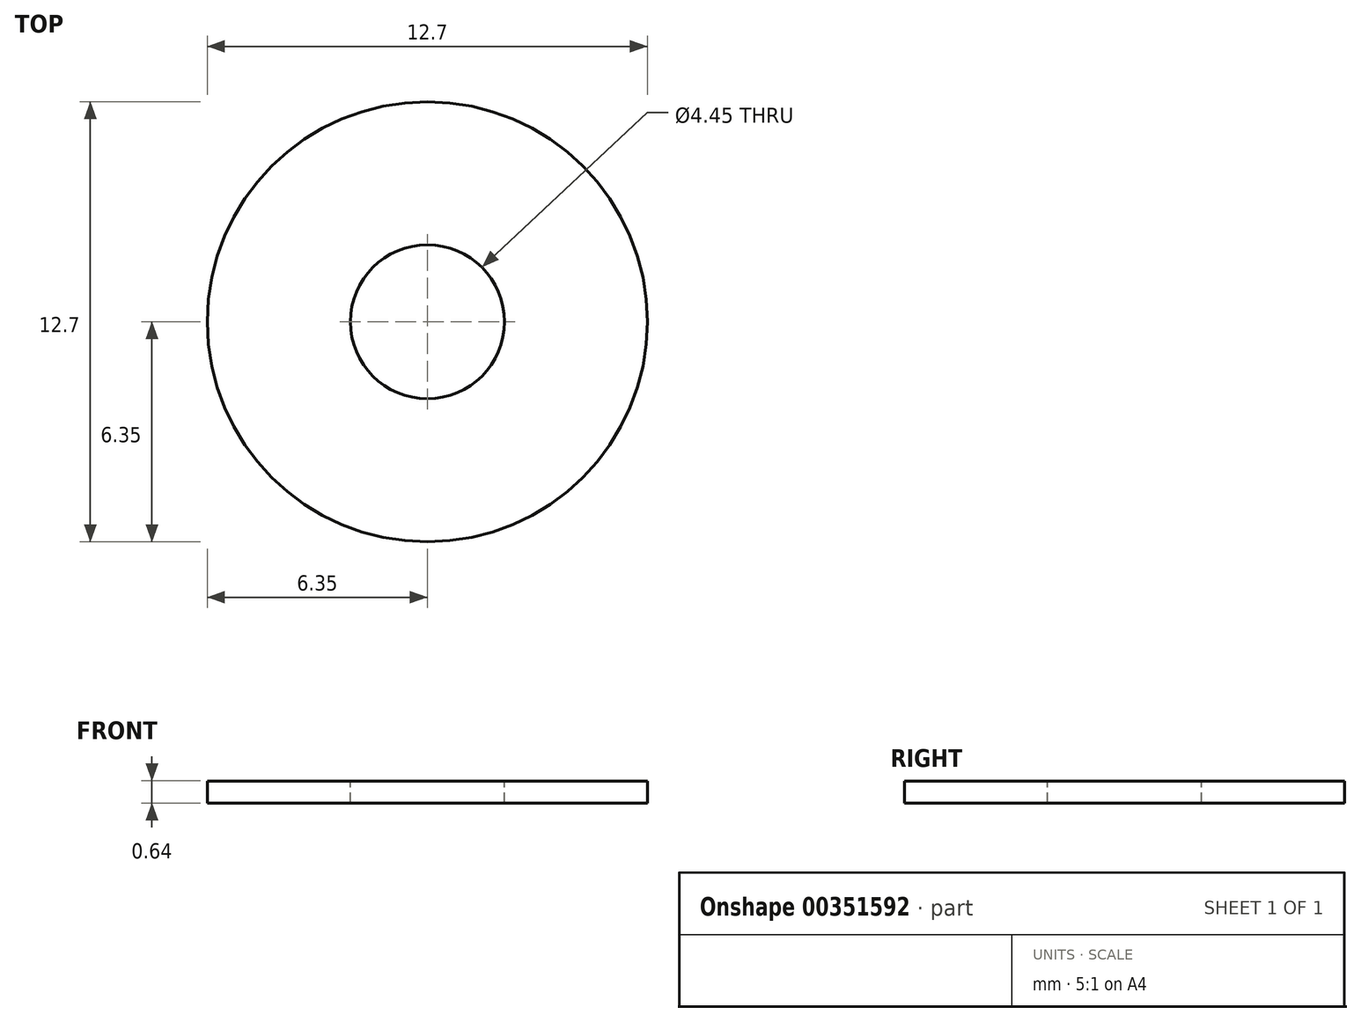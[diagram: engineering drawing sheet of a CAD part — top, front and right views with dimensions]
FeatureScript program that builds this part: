
annotation { "Feature Type Name" : "Feature", "Feature Type Description" : "" }
export const myFeature = defineFeature(function(context is Context, id is Id, definition is map)
    precondition{}
    {
        {
            var Q0;
            Q0=qCreatedBy(makeId("Top.planeOp"),FACE);
            var sketch = newSketch(context, id + "F0", { "sketchPlane" : qUnion([Q0])});
            skCircle(sketch, "E0", {"center": v(0, 0) * mm, "radius": 6.35 * mm});
            skSolve(sketch);
        }
        {
            var Q0;
            Q0 = qSketchRegion(id + "F0", true);
            extrude(context, id + "F1", {"entities" : qUnion([Q0]), "depth" : 0.64 * mm});
        }
        {
            var Q0;
            Q0=makeQuery(id+"F1.opExtrude","CAP_FACE",FACE,{"disambiguationData":[OSD([sQuery(id+"F0.wireOp",EDGE,"E0")])],"isStart":false});
            var sketch = newSketch(context, id + "F2", { "sketchPlane" : qUnion([Q0])});
            skCircle(sketch, "E1", {"center": v(0, 0) * mm, "radius": 2.22 * mm});
            skSolve(sketch);
        }
        {
            var Q0;
            Q0 = qSketchRegion(id + "F2", true);
            var Q1;
            Q1=makeQuery(id+"F1.opExtrude","CAP_FACE",FACE,{"disambiguationData":[OSD([sQuery(id+"F0.wireOp",EDGE,"E0")])],"isStart":true});
            extrude(context, id + "F3", {"entities" : qUnion([Q0]), "operationType" : NewBodyOperationType.REMOVE, "endBound" : BoundingType.UP_TO_SURFACE, "oppositeDirection" : true, "endBoundEntityFace" : qUnion([Q1]), "depth" : 25.4 * mm});
        }
    });
